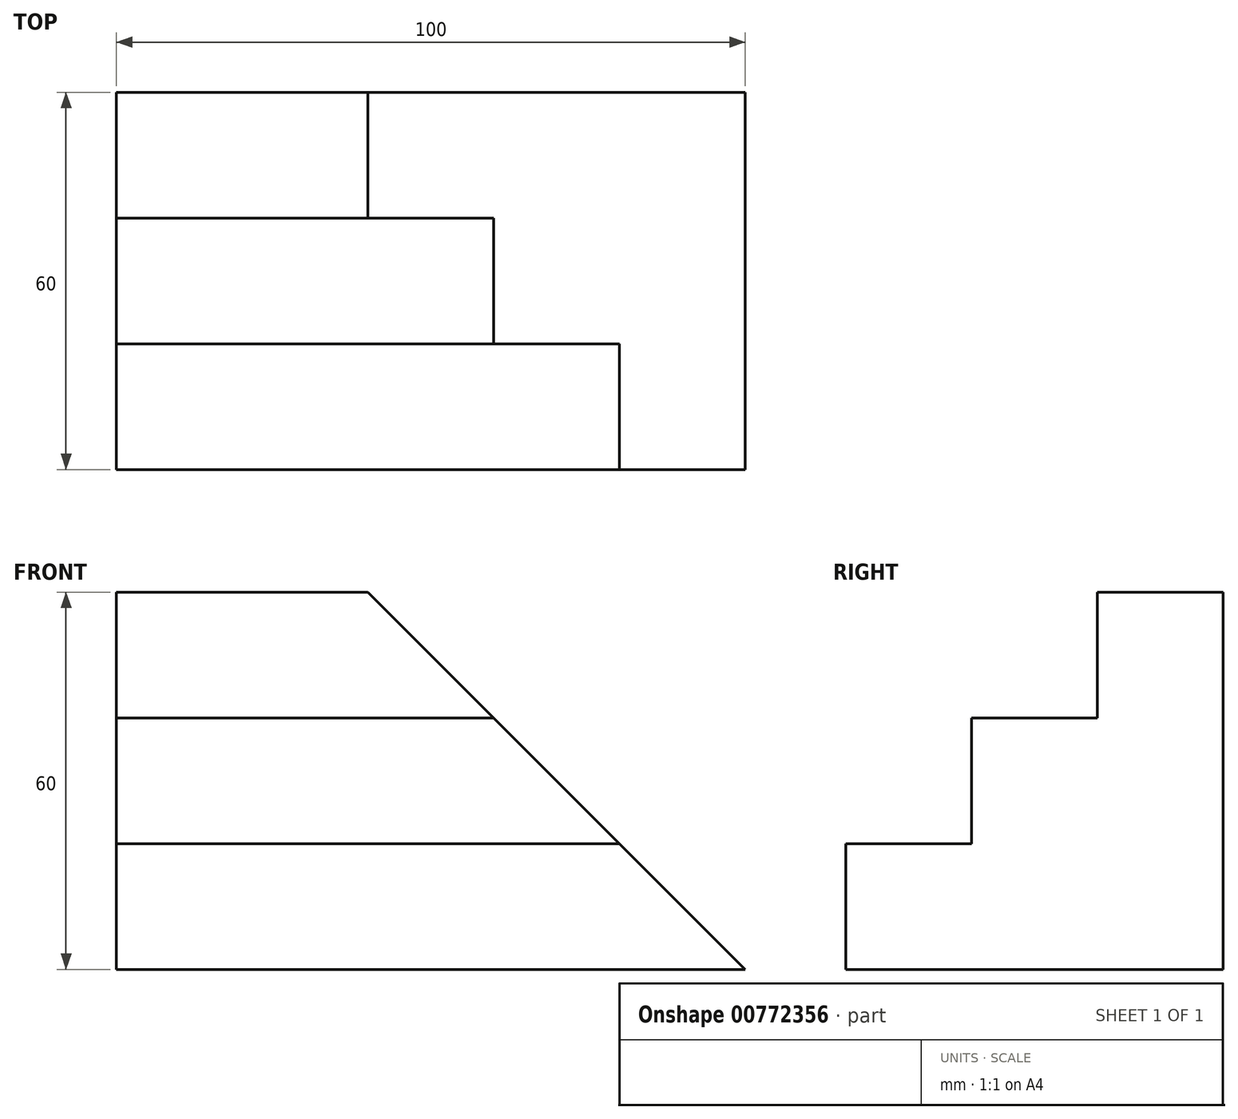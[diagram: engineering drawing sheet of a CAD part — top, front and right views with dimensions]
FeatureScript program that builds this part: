
annotation { "Feature Type Name" : "Feature", "Feature Type Description" : "" }
export const myFeature = defineFeature(function(context is Context, id is Id, definition is map)
    precondition{}
    {
        {
            var Q0;
            Q0=qCreatedBy(makeId("Right.planeOp"),FACE);
            var sketch = newSketch(context, id + "F0", { "sketchPlane" : qUnion([Q0])});
            skLineSegment(sketch, "E0", {"start": v(0, 0) * mm, "end": v(0, 60) * mm});
            skLineSegment(sketch, "E1", {"start": v(0, 60) * mm, "end": v(-20, 60) * mm});
            skLineSegment(sketch, "E2", {"start": v(-20, 60) * mm, "end": v(-20, 40) * mm});
            skLineSegment(sketch, "E3", {"start": v(-20, 40) * mm, "end": v(-40, 40) * mm});
            skLineSegment(sketch, "E4", {"start": v(-40, 40) * mm, "end": v(-40, 20) * mm});
            skLineSegment(sketch, "E5", {"start": v(-40, 20) * mm, "end": v(-60, 20) * mm});
            skLineSegment(sketch, "E6", {"start": v(-60, 20) * mm, "end": v(-60, 0) * mm});
            skLineSegment(sketch, "E7", {"start": v(-60, 0) * mm, "end": v(0, 0) * mm});
            skSolve(sketch);
        }
        {
            var Q0;
            Q0 = qSketchRegion(id + "F0", true);
            extrude(context, id + "F1", {"entities" : qUnion([Q0]), "depth" : 100 * mm, "offsetDistance" : 25 * mm});
        }
        {
            var Q0;
            Q0=makeQuery(id+"F1.opExtrude","CAP_EDGE",EDGE,{"disambiguationData":[OSD([sQuery(id+"F0.wireOp",EDGE,"E1")])],"isStart":false});
            chamfer(context, id + "F2", {"entities" : qUnion([Q0]), "chamferType" : ChamferType.TWO_OFFSETS, "width1" : 60 * mm, "oppositeDirection" : false, "width2" : 60 * mm, "tangentPropagation" : true});
        }
    });
